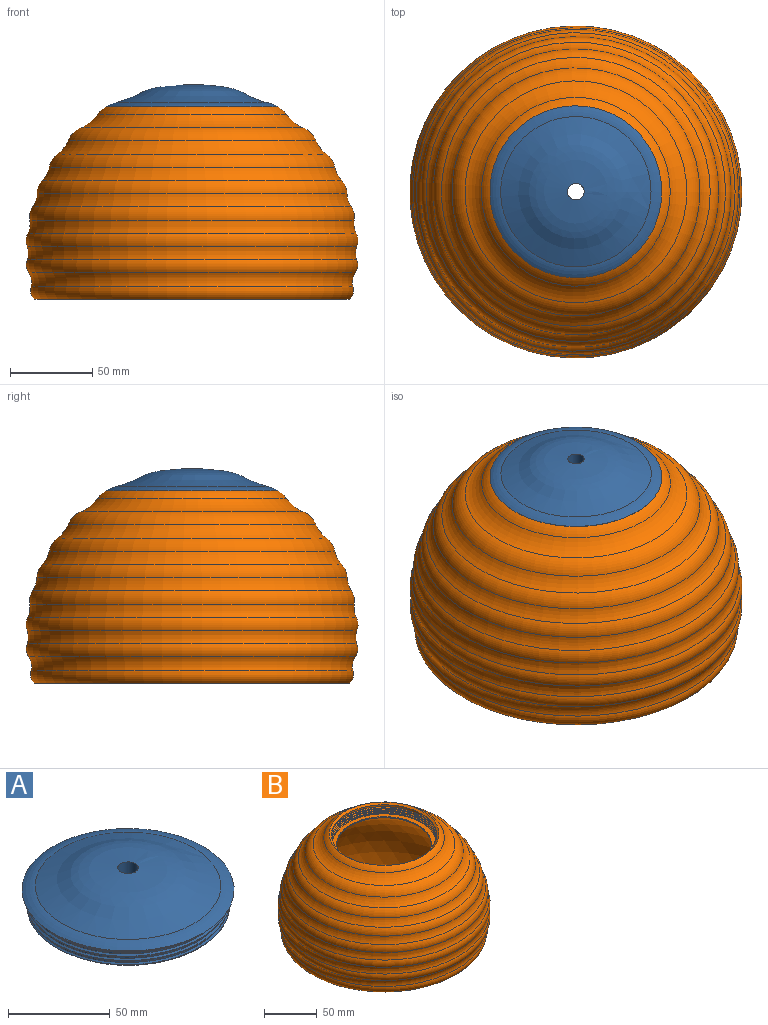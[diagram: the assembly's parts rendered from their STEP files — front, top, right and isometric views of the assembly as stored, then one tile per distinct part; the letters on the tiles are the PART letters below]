
ASSEMBLY  parts=2 mates=1
PART A: 11 faces, bbox 120.4x120.4x24.9 mm
  f0: cylinder r=49mm len=98mm, axis (0,0,1), area 745.3mm2, adj f1,f2,f8,f9
  f1: bspline ~115.24x99.8mm, area 1152.8mm2, adj f0,f3,f8,f9
  f2: bspline ~115.24x99.8mm, area 1153.3mm2, adj f0,f3,f8,f9
  f3: cylinder r=49.9mm len=99.8mm, axis (0,0,-1), area 288.1mm2, adj f1,f2,f8,f9
  f4: sphere r=92.5mm, area 5733.3mm2, adj f5,f10
  f5: cylinder r=5mm len=15.01mm, axis (0,0,1), area 471.6mm2, adj f4,f6
  f6: revolved ~91.19x91.19mm, area 6849.5mm2, adj f5,f7
  f7: torus R=42.83mm, axis (0,0,1), area 2140.7mm2, adj f6,f8
  f8: cone r=52.1mm half-angle=50deg, axis (0,0,1), area 1137.3mm2, adj f0,f1,f2,f3,f7
  f9: cone r=49.9mm half-angle=50deg, axis (0,0,1), area 587.4mm2, adj f0,f1,f2,f3,f10
  f10: plane 95.79x95.79mm, normal (0,0,-1), area 1709.2mm2, adj f4,f9
PART B: 28 faces, bbox 223.2x223.2x127.6 mm
  f0: cylinder r=50mm len=100mm, axis (0,0,1), area 1194.6mm2, adj f1,f19,f21,f24,f25
  f1: cone r=52.1mm half-angle=50deg, axis (0,0,1), area 880.1mm2, adj f0,f2
  f2: torus R=42.83mm, axis (0,0,1), area 2398.6mm2, adj f1,f3
  f3: torus R=76.1mm, axis (0,0,1), area 5052.1mm2, adj f2,f4
  f4: torus R=62.1mm, axis (0,0,1), area 5205.7mm2, adj f3,f5
  f5: torus R=93.94mm, axis (0,0,1), area 5051.1mm2, adj f4,f6
  f6: torus R=74.23mm, axis (0,0,1), area 5180.6mm2, adj f5,f7
  f7: torus R=104.49mm, axis (0,0,1), area 5054.2mm2, adj f6,f8
  f8: torus R=82.67mm, axis (0,0,1), area 5180.8mm2, adj f7,f9
  f9: torus R=110.28mm, axis (0,0,1), area 5060.9mm2, adj f8,f10
  f10: torus R=88.34mm, axis (0,0,1), area 5197.6mm2, adj f9,f11
  f11: torus R=112.45mm, axis (0,0,1), area 5072.6mm2, adj f10,f12
  f12: torus R=91.58mm, axis (0,0,1), area 5232.9mm2, adj f11,f13
  f13: torus R=111.53mm, axis (0,0,1), area 5092.8mm2, adj f12,f14
  f14: torus R=92.48mm, axis (0,0,1), area 5296.7mm2, adj f13,f15
  f15: torus R=107.78mm, axis (0,0,1), area 5129.7mm2, adj f14,f16
  f16: torus R=90.92mm, axis (0,0,1), area 5411.9mm2, adj f15,f17
  f17: plane 190.79x190.79mm, normal (0,0,-1), area 2734.9mm2, adj f16,f27
  f18: sphere r=92.5mm, area 59400.9mm2, adj f26,f27
  f19: plane 100.09x99.95mm, normal (0,0,1), area 1367.3mm2, adj f0,f20,f21,f22,f23,f24
  f20: cone r=44.74mm half-angle=14.5deg, axis (0,0,1), area 163.6mm2, adj f19,f26
  f21: bspline ~115.47x100mm, area 16.3mm2, adj f0,f19,f22,f25
  f22: bspline ~115.45x99.98mm, area 1393.8mm2, adj f19,f21,f23,f25
  f23: cylinder r=49.1mm len=98.2mm, axis (0,0,-1), area 316.7mm2, adj f19,f22,f24,f25
  f24: bspline ~115.47x100mm, area 1259.5mm2, adj f0,f19,f23,f25
  f25: plane 1.8x0.9mm, normal (0,1,0), area 0.9mm2, adj f0,f21,f22,f23,f24
  f26: cone r=45.27mm half-angle=23.1deg, axis (0,0,-1), area 269.6mm2, adj f18,f20
  f27: cone r=90.72mm half-angle=38.3deg, axis (0,0,-1), area 695.4mm2, adj f17,f18
PLACE A t=(-110.62,73.53,118.46)mm
PLACE B t=(-110.62,73.53,118.36)mm
MATE fastened B.f20 <-> A.f0  axis (0,0,1) through (-110.62,73.53,192.96)mm
